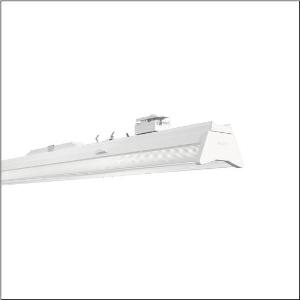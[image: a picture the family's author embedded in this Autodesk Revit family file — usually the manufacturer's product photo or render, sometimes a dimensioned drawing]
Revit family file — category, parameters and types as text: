
# Revit family: licross_r__21_performance_ho_52td16mn4e5m_6ed4
name_source: partatom
category: Lighting Fixtures
units: mm (PartAtom-declared; Revit-internal decimal feet)

## family parameters
Cut with Voids When Loaded = No
Host = Face
Light Source = No
Part Type = Normal
Room Calculation Point = No
Round Connector Dimension = Use Diameter
Shared = No

## types (1)
- --- (1 x LED, 14970 lm, 83.2 W, 4000K)
    Apparent Load = 83 VA
    CIE Flux Codes = 63 87 95 78 100
    Color Rendering = 80
    Color Temperature = 4000K
    Default Elevation = 1800 mm
    Description = Licross® 21 Performance HO, luminaire insert, of sheet steel, galvanised, coil coated, white, length: 1.500mm, width: 120mm, height: 123mm, LED rated luminous flux: 14.970lm, light colour: 840, control gear: ON/OFF Multilumen, with plug, 3-pole, with phase selection, mains connection: 220..240V, AC, 50/60Hz, rated input power: 83W, halogen-free wiring, primary light control with lens, of plastic, primary optical cover: cover, of PMMA, light emission: direct/indirect distribution, primary light characteristic: symmetric, protection rating (complete): IP54, insulation class (complete): insulation class I (protective earthing), certification: CE, ENEC, UKCA, protection symbol: D if used in an environment with non-conductive dust loads with corresponding accessories, impact resistance: IK06, permissible ambient temperature for indoor applications: -35..+35°C, corresponds to IFS (International Featured Standards) requirements for safety and quality in the food industry, reducing of maximum allowable ambient temperature of 5°C with ceiling mounting, LABS conformity tested according to VDMA 24364:2018-05, packaging unit: 1 piece
    Height = 114 mm
    Lamp = 1 x LED
    Lamp Light Flux = 14970 lm
    Lamp Power = 83.2 W
    Lamp count = 1
    Length = 1500 mm
    Luminous efficacy = 180 lm/W
    Manufacturer = Siteco
    ModVariant = No
    Model = 52TD16MN4E5M
    Mounting Place = Ceiling
    Mounting Type = Pendant
    Number of Poles = 1
    OnlyDefault = Yes
    Power Factor = 1
    Product Name = Licross® 21 Performance HO
    Product group = luminaire insert
    ProductGroupID = 901
    Protection Class = Protection class I
    Protection Degree = IP 54
    RLX_Detail_Level = 1
    RLX_Emergency_Light_Flux = 0 lm
    RLX_Emergency_Type = 0
    RLX_Emergency_Type_DB = No
    RlxData = <blob elided: 31733 chars, md5=f699deb4>
    Socket = socket
    Standby Power = 0 W
    System Light Flux = 14970 lm
    System Power = 83 W
    Type Comments = factory setting: luminous flux: 100 % | (A | C | E) | 195 mA
    Type Image = l_1256138.jpg
    URL = http://relux.com
    VarID = @adj_039367
    Voltage = 0 V
    Weight = 0.00 kg
    Width = 120 mm

## geometry (parser evidence)
native form markers: Blend x4, Sweep x10
no freeform markers — native parametric forms only
